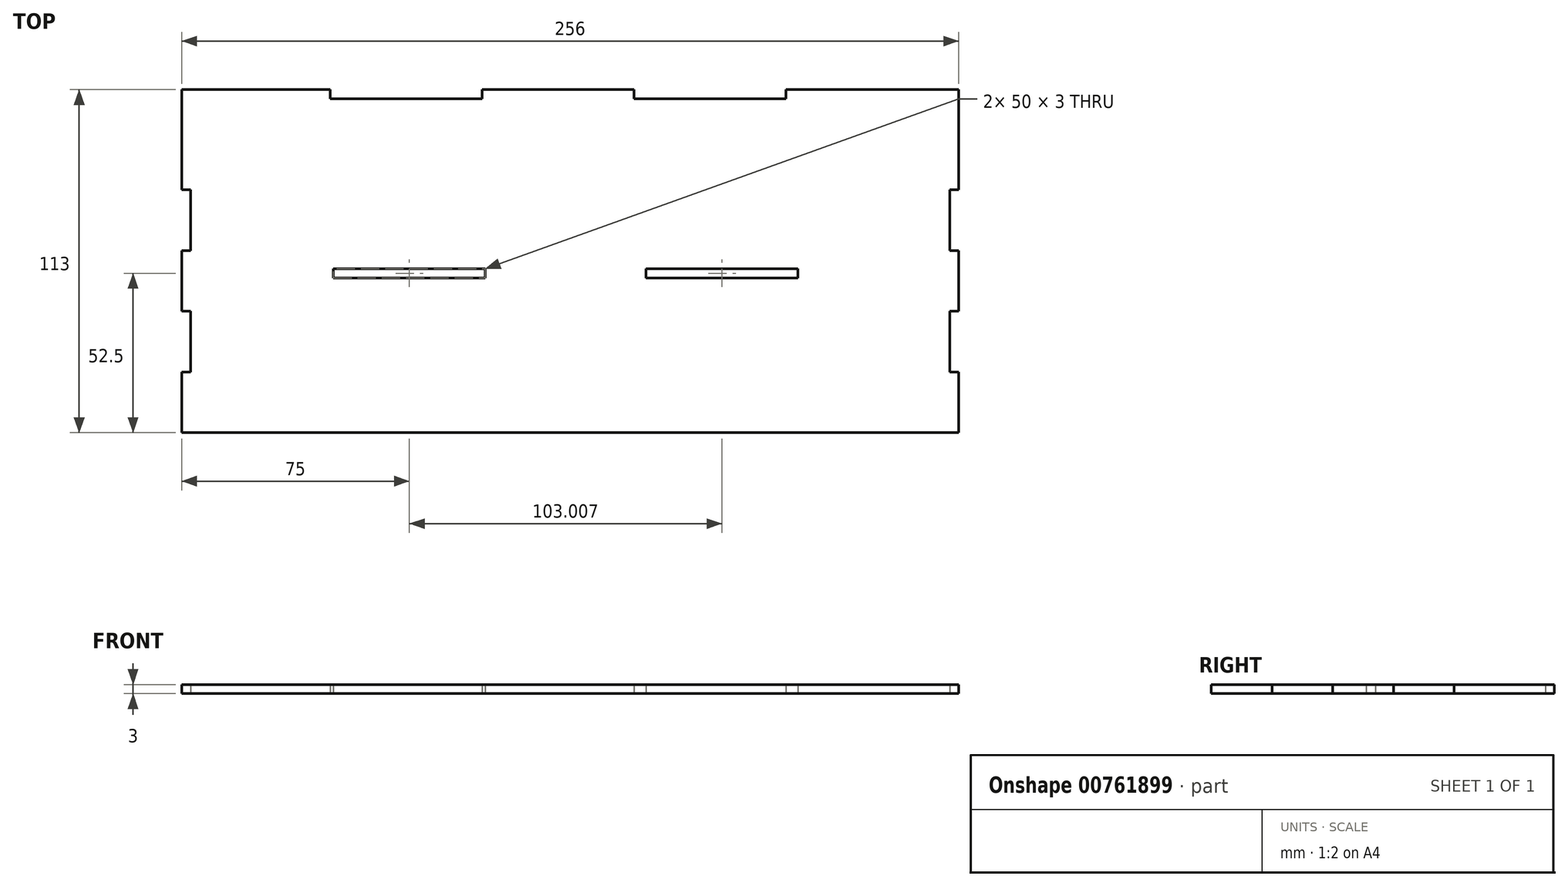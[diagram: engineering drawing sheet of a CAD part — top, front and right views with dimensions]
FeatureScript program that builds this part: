
annotation { "Feature Type Name" : "Feature", "Feature Type Description" : "" }
export const myFeature = defineFeature(function(context is Context, id is Id, definition is map)
    precondition{}
    {
        {
            var Q0;
            Q0=qCreatedBy(makeId("Top.planeOp"),FACE);
            var sketch = newSketch(context, id + "F0", { "sketchPlane" : qUnion([Q0])});
            skLineSegment(sketch, "E0.bottom", {"start": v(-250, 0) * mm, "end": v(0, 0) * mm});
            skLineSegment(sketch, "E0.top", {"start": v(-250, -110) * mm, "end": v(0, -110) * mm});
            skLineSegment(sketch, "E0.left", {"start": v(-250, 0) * mm, "end": v(-250, -110) * mm});
            skLineSegment(sketch, "E0.right", {"start": v(0, 0) * mm, "end": v(0, -110) * mm});
            skLineSegment(sketch, "E1.bottom", {"start": v(-204, 0) * mm, "end": v(-250, 0) * mm});
            skLineSegment(sketch, "E1.top", {"start": v(-204, 3) * mm, "end": v(-250, 3) * mm});
            skLineSegment(sketch, "E1.left", {"start": v(-204, 0) * mm, "end": v(-204, 3) * mm});
            skLineSegment(sketch, "E1.right", {"start": v(-250, 0) * mm, "end": v(-250, 3) * mm});
            skLineSegment(sketch, "E2", {"start": v(-204, 0) * mm, "end": v(-154, 0) * mm});
            skLineSegment(sketch, "E3.bottom", {"start": v(-154, 0) * mm, "end": v(-104, 0) * mm});
            skLineSegment(sketch, "E3.top", {"start": v(-154, 3) * mm, "end": v(-104, 3) * mm});
            skLineSegment(sketch, "E3.left", {"start": v(-154, 0) * mm, "end": v(-154, 3) * mm});
            skLineSegment(sketch, "E3.right", {"start": v(-104, 0) * mm, "end": v(-104, 3) * mm});
            skLineSegment(sketch, "E4", {"start": v(-104, 0) * mm, "end": v(-54, 0) * mm});
            skLineSegment(sketch, "E5.bottom", {"start": v(-54, 0) * mm, "end": v(0, 0) * mm});
            skLineSegment(sketch, "E5.top", {"start": v(-54, 3) * mm, "end": v(0, 3) * mm});
            skLineSegment(sketch, "E5.left", {"start": v(-54, 0) * mm, "end": v(-54, 3) * mm});
            skLineSegment(sketch, "E5.right", {"start": v(0, 0) * mm, "end": v(0, 3) * mm});
            skLineSegment(sketch, "E6.bottom", {"start": v(-250, -110) * mm, "end": v(-253, -110) * mm});
            skLineSegment(sketch, "E6.top", {"start": v(-250, -90) * mm, "end": v(-253, -90) * mm});
            skLineSegment(sketch, "E6.left", {"start": v(-250, -110) * mm, "end": v(-250, -90) * mm});
            skLineSegment(sketch, "E6.right", {"start": v(-253, -110) * mm, "end": v(-253, -90) * mm});
            skLineSegment(sketch, "E7", {"start": v(-250, -90) * mm, "end": v(-250, -70) * mm});
            skLineSegment(sketch, "E8.bottom", {"start": v(-250, -70) * mm, "end": v(-253, -70) * mm});
            skLineSegment(sketch, "E8.top", {"start": v(-250, -50) * mm, "end": v(-253, -50) * mm});
            skLineSegment(sketch, "E8.left", {"start": v(-250, -70) * mm, "end": v(-250, -50) * mm});
            skLineSegment(sketch, "E8.right", {"start": v(-253, -70) * mm, "end": v(-253, -50) * mm});
            skLineSegment(sketch, "E9", {"start": v(-250, -50) * mm, "end": v(-250, -30) * mm});
            skLineSegment(sketch, "E10.bottom", {"start": v(-250, -30) * mm, "end": v(-253, -30) * mm});
            skLineSegment(sketch, "E10.top", {"start": v(-250, 3) * mm, "end": v(-253, 3) * mm});
            skLineSegment(sketch, "E10.left", {"start": v(-250, -30) * mm, "end": v(-250, 3) * mm});
            skLineSegment(sketch, "E10.right", {"start": v(-253, -30) * mm, "end": v(-253, 3) * mm});
            skLineSegment(sketch, "E11.bottom", {"start": v(0, -110) * mm, "end": v(3, -110) * mm});
            skLineSegment(sketch, "E11.top", {"start": v(0, -90) * mm, "end": v(3, -90) * mm});
            skLineSegment(sketch, "E11.left", {"start": v(0, -110) * mm, "end": v(0, -90) * mm});
            skLineSegment(sketch, "E11.right", {"start": v(3, -110) * mm, "end": v(3, -90) * mm});
            skLineSegment(sketch, "E12", {"start": v(0, -90) * mm, "end": v(0, -70) * mm});
            skLineSegment(sketch, "E13.bottom", {"start": v(0, -70) * mm, "end": v(3, -70) * mm});
            skLineSegment(sketch, "E13.top", {"start": v(0, -50) * mm, "end": v(3, -50) * mm});
            skLineSegment(sketch, "E13.left", {"start": v(0, -70) * mm, "end": v(0, -50) * mm});
            skLineSegment(sketch, "E13.right", {"start": v(3, -70) * mm, "end": v(3, -50) * mm});
            skLineSegment(sketch, "E14", {"start": v(0, -50) * mm, "end": v(0, -30) * mm});
            skLineSegment(sketch, "E15.bottom", {"start": v(0, -30) * mm, "end": v(3, -30) * mm});
            skLineSegment(sketch, "E15.top", {"start": v(0, 3) * mm, "end": v(3, 3) * mm});
            skLineSegment(sketch, "E15.left", {"start": v(0, -30) * mm, "end": v(0, 3) * mm});
            skLineSegment(sketch, "E15.right", {"start": v(3, -30) * mm, "end": v(3, 3) * mm});
            skLineSegment(sketch, "E16.bottom", {"start": v(-203, -56) * mm, "end": v(-153, -56) * mm});
            skLineSegment(sketch, "E16.top", {"start": v(-203, -59) * mm, "end": v(-153, -59) * mm});
            skLineSegment(sketch, "E16.left", {"start": v(-203, -56) * mm, "end": v(-203, -59) * mm});
            skLineSegment(sketch, "E16.right", {"start": v(-153, -56) * mm, "end": v(-153, -59) * mm});
            skLineSegment(sketch, "E17.bottom", {"start": v(-100, -56) * mm, "end": v(-50, -56) * mm});
            skLineSegment(sketch, "E17.top", {"start": v(-100, -59) * mm, "end": v(-50, -59) * mm});
            skLineSegment(sketch, "E17.left", {"start": v(-100, -56) * mm, "end": v(-100, -59) * mm});
            skLineSegment(sketch, "E17.right", {"start": v(-50, -56) * mm, "end": v(-50, -59) * mm});
            skSolve(sketch);
        }
        {
            var Q0;
            Q0 = qSketchRegion(id + "F0", true);
            extrude(context, id + "F1", {"entities" : qUnion([Q0]), "depth" : 3 * mm, "offsetDistance" : 25.4 * mm});
        }
    });
